# Revit family: Haworth_Epure_Fan-ShapedDesk_EU_PRELIMINARY
name_source: partatom
category: Furniture
units: mm (PartAtom-declared; Revit-internal decimal feet)

## family parameters
Always vertical = Yes
Cut with Voids When Loaded = No
OmniClass Number = 23.40.70.14.64.11
OmniClass Title = Office Furniture
Room Calculation Point = No
Shared = No
Work Plane-Based = No

## types (5) — shared parameters
Actual Depth = 100 cm
Actual Height = 73 cm
Assembly Code = E2020200
Description = Haworth - Epure - Wave Desk
Flip Top Finish = Haworth _ Paint _ Metallic Silver
Leg Height = 70 cm
Manufacturer = Haworth
Model = EUWD1X10
Revision Number = 1
Size = Verify Final Dim.w/ Haworth
Trim Finish = Haworth _ Metal _ Structured White EC
URL = https://www.haworth.com
URL - Product = https://www.haworth.com
Warranty = http://www.haworth.com

## per-type parameters (varying)
| type | Accessory Kit | Actual Width | Cable Outlet | Flip Top Cable Outlet | Large | Medium | No Accessory Kit | Rounded Corners | Small | Squared Corners |
| 160 x 100 - rounded | No | 160 cm | No | No | No | No | Yes | Yes | Yes | No |
| 180 x 100 - rounded | Yes | 180 cm | No | Yes | No | Yes | No | Yes | No | No |
| 160 x 100 - squared | Yes | 160 cm | Yes | No | No | No | No | No | Yes | Yes |
| 180 x 100 - squared | Yes | 180 cm | Yes | No | No | Yes | No | No | No | Yes |
| 180 x 100 - squared - Wood | Yes | 180 cm | No | Yes | Yes | No | No | No | No | Yes |

type visibility flags (boolean, named after types; folded from table):
- 160 x 100 - rounded: Yes: 160 x 100 - rounded
- 180 x 100 - rounded: Yes: 180 x 100 - rounded
- 160 x 100 - squared: Yes: 160 x 100 - squared
- 180 x 100 - squared: Yes: 180 x 100 - squared
- 180 x 100 - squared - Wood: Yes: 180 x 100 - squared wood

## geometry (parser evidence)
native form markers: Sweep x13
no freeform markers — native parametric forms only
